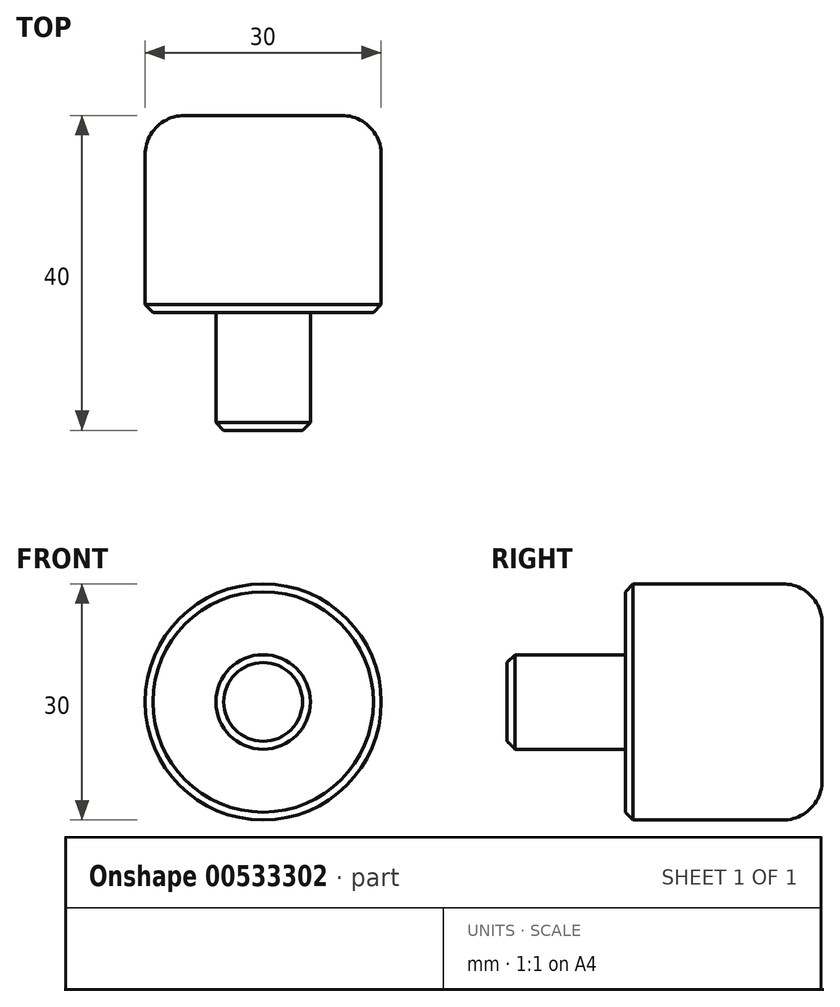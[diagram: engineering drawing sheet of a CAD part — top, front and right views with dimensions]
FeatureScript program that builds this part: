
annotation { "Feature Type Name" : "Feature", "Feature Type Description" : "" }
export const myFeature = defineFeature(function(context is Context, id is Id, definition is map)
    precondition{}
    {
        {
            var Q0;
            Q0=qCreatedBy(makeId("Front.planeOp"),FACE);
            var sketch = newSketch(context, id + "F0", { "sketchPlane" : qUnion([Q0])});
            skCircle(sketch, "E0", {"center": v(0, 0) * mm, "radius": 15 * mm});
            skSolve(sketch);
        }
        {
            var Q0;
            Q0=makeQuery(id+"F0.imprint","IMPRINT",FACE,{"disambiguationData":[TD([[makeQuery(id+"F0.imprint","IMPRINT",EDGE,{"derivedFrom":sQuery(id+"F0.wireOp",EDGE,"E0")}),1.0]])]});
            extrude(context, id + "F1", {"entities" : qUnion([Q0]), "depth" : 25 * mm, "offsetDistance" : 25.4 * mm});
        }
        {
            var Q0;
            Q0=makeQuery(id+"F1.opExtrude","CAP_FACE",FACE,{"disambiguationData":[OSD([sQuery(id+"F0.wireOp",EDGE,"E0")])],"isStart":false});
            var sketch = newSketch(context, id + "F2", { "sketchPlane" : qUnion([Q0])});
            skCircle(sketch, "E1", {"center": v(0, 0) * mm, "radius": 6 * mm});
            skSolve(sketch);
        }
        {
            var Q0;
            Q0=qSketchRegion(id+"F2",true);
            extrude(context, id + "F3", {"entities" : qUnion([Q0]), "operationType" : NewBodyOperationType.ADD, "depth" : 15 * mm, "offsetDistance" : 25.4 * mm});
        }
        {
            var Q0;
            Q0=makeQuery(id+"F1.opExtrude","CAP_EDGE",EDGE,{"disambiguationData":[OSD([sQuery(id+"F0.wireOp",EDGE,"E0")])],"isStart":true});
            fillet(context, id + "F4", {"entities" : qUnion([Q0]), "radius" : 5 * mm, "tangentPropagation" : true, "allowEdgeOverflow" : false});
        }
        {
            var Q0;
            Q0=makeQuery(id+"F3.opExtrude","CAP_EDGE",EDGE,{"disambiguationData":[OSD([sQuery(id+"F2.wireOp",EDGE,"E1")])],"isStart":false});
            var Q1;
            Q1=makeQuery(id+"F3.opExtrude","CAP_EDGE",EDGE,{"disambiguationData":[OSD([sQuery(id+"F2.wireOp",EDGE,"E1")])],"isStart":true});
            var Q2;
            Q2=makeQuery(id+"F1.opExtrude","CAP_EDGE",EDGE,{"disambiguationData":[OSD([sQuery(id+"F0.wireOp",EDGE,"E0")])],"isStart":false});
            chamfer(context, id + "F5", {"entities" : qUnion([Q0, Q1, Q2]), "width" : 1 * mm, "tangentPropagation" : true});
        }
    });
